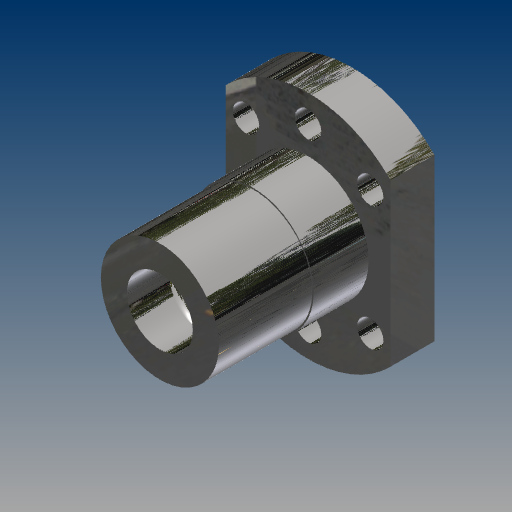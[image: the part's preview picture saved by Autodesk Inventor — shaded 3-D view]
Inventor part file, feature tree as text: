
AUTODESK INVENTOR PART (.ipt)
format: ipt  version: 2021 (Build 250183000, 183)  size: 448,000 bytes
history: native  units: in
note: dims shown in document units (in); Inventor stores cm internally (conversion verified against a paired STEP export)
features: sketch x6, extrude x5, projected_geometry x4, hole x2, pattern_circular x1, helix x1
ambient origin geometry x8: Origin, YZ Plane, XZ Plane, XY Plane, X Axis, Y Axis, Z Axis, Center Point
bodies: Solid1 (feature_tree)
feature tree (19):
  extrude  "Extrusion1"  Depth=0.315in TaperAngle=0.0deg
  extrude  "Extrusion2"  Depth=0.3937in TaperAngle=0.0deg
  extrude  "Extrusion3"  Depth=0.6693in TaperAngle=0.0deg
  extrude  "Extrusion4"  Depth=0.6693in TaperAngle=0.0deg
  hole  "Hole1"  [1 undecoded]
  pattern_circular  "Circular Pattern1"  Count=2 Angle=360.0deg
  hole  "Hole2"  [1 undecoded]
  sketch  "Sketch6"  dims[d17=1.2598in d19=0.189in d20=0.75in d21=0.375in d22=0.25in d23=0.5635in d24=1.0in d25=0.8108in d26=0.7874in d27=360.0deg d29=1.0in d30=1.0in d31=0.4724in d32=0.75in d33=0.375in d34=0.25in d35=0.5635in d36=1.0in d37=0.8108in d38=0.1181in d40=0.5315in d41=0.1575in d42=0.9843in d43=0.3937in d44=0.0in d45=90.0deg d46=90.0deg d47=0.0in d48=0.0in d49=0.2362in d50=0.0197in d51=0.0in]
  helix  "Coil1"  [1 undecoded]
  extrude  "Extrusion5"  Depth=0.0197in
  sketch  "Sketch1"  dims[d0=1.6535in d2=0.315in d3=0.0in]
  sketch  "Sketch2"  dims[d4=0.8661in d6=0.3937in d7=0.0in]
  projected_geometry  "Projected Loop1"
  sketch  "Sketch3"  dims[d8=0.8465in d10=0.6693in d11=0.0in]
  sketch  "Sketch4"  dims[d12=1.1811in d13=0.6693in d14=0.0in]
  projected_geometry  "Projected Loop2"
  sketch  "Sketch5"  dims[d15=45.0deg d16=45.0deg]
  projected_geometry  "Projected Loop3"
  projected_geometry  "Project Cut Edges1"
note: 3 required parameter values undecoded (feature->parameter linkage not recoverable at this tier; creation-order binding heuristic only, values carry confidence <= 0.55)
